# Revit family: Domotics-DomesticRanges-GEWISS-CHORUS_POWER-SOCKET-OUTLET_ITA_3xP11P17_16A
name_source: partatom
category: Apparecchi elettrici
revit_build: Autodesk Revit 2016 (Build: 20161004_0715(x64)
units: mm (PartAtom-declared; Revit-internal decimal feet)

## family parameters
Condiviso = Sì
Host = Superficie
Mantenere orientamento annotazione = Sì
Numero OmniClass = 23.80.50.14
Punto di calcolo locali = Sì
Quota connettore circolare = Usa diametro
Taglio con vuoti quando caricato = Sì
Tipo di parte = Normale
Titolo OmniClass = Plug Connectors

## types (3) — shared parameters
Breaking capacity: = 1.25 In (100 position changes)
Carico apparente = 0 VA
Catalogue = DOMOTICS
Catalogue Range = CHORUS - DOMESTIC RANGE
Category = Triple socket-outlet
Characteristics = With safety shields
Description. = Triple socket-outlet
Description: = 3x2P+E - 16A Dual amperage
Electrocod = 0131
For plug pins = Ã˜ 4 / 5 mm
Glow Wire Test = 850°C
IDF = f29b0997-185e-4d91-b09a-3b50a3e9a6bf
IDT = 509edcbc-8745-4f75-b27e-7ee1dae8fffa
Immagine tipo = GW14209.jpg
Insulation resistance = > 5 MOhm
Larghezza presa = 69 mm  [stored 0.226378 ft]
N. poli = 1
No. Chorus modules = 3
No. Chorus modules: = 3
Produttore = GEWISS S.p.A.
Prolonged operation (no.of position changes) = 10.000 at In 250 V ac cosÃ˜=0,8
Prospetto di default = 1219 mm
Resistance at test voltage = 2000 V at 50 Hz for 1 minute
SEO = Socket outlet
Simbolo = SIMBOLO PRESE TRIPLE : PRESA TRIPLA
Socket-out type = P11-P17
Standard = English
Standard: = English
Standard; = IEC 60884-1
Technical sheet = https://www.gewiss.com
Terminal grip on cable traction = > 50 N
Terminal tightening capacity flexible cables (mm2) = min. 0,75 - max. 2x4
Terminal tightening capacity rigid cables (mm2) = min. 0,5 - max. 2x2,5
Thermo-pressure with ball = 125
Tipo = CHORUS PRESE TRIPLE ITA P11-17 16A_BASE : TITANIO
URL = https://www.gewiss.com
Version file RFA = 19.0
Volt = 230 V
Voltage = 250 V ac
Voltage: = 250 V ac
Wiring terminals = With screw

## per-type parameters (varying)
| type | Colour | Descrizione | EAN code | Modello |
| GW12209 - Black | Black | TRIP SOC, 2P+E 16A P17-11 D.AM IT/G ST B | 8011564269514 | GW12209 |
| GW10209 - White | White | 3XS. OUT. 2P+E 16A P17-11 D.AM IT WH | 8011564259874 | GW10209 |
| GW14209 - Titanium | Titanium | TRIP SOCKET 2P+E 16A P17-11 D.AM IT ST T | 8011564266346 | GW14209 |

note: source unit labels omitted for Thermo-pressure with ball — the stored unit's dimension contradicts the parameter name (converter mislabeling)

note: [stored X ft] marks values corroborated as IEEE doubles in the binary element streams (Revit-internal decimal feet)

## geometry (parser evidence)
native form markers: Sweep x2
no freeform markers — native parametric forms only
